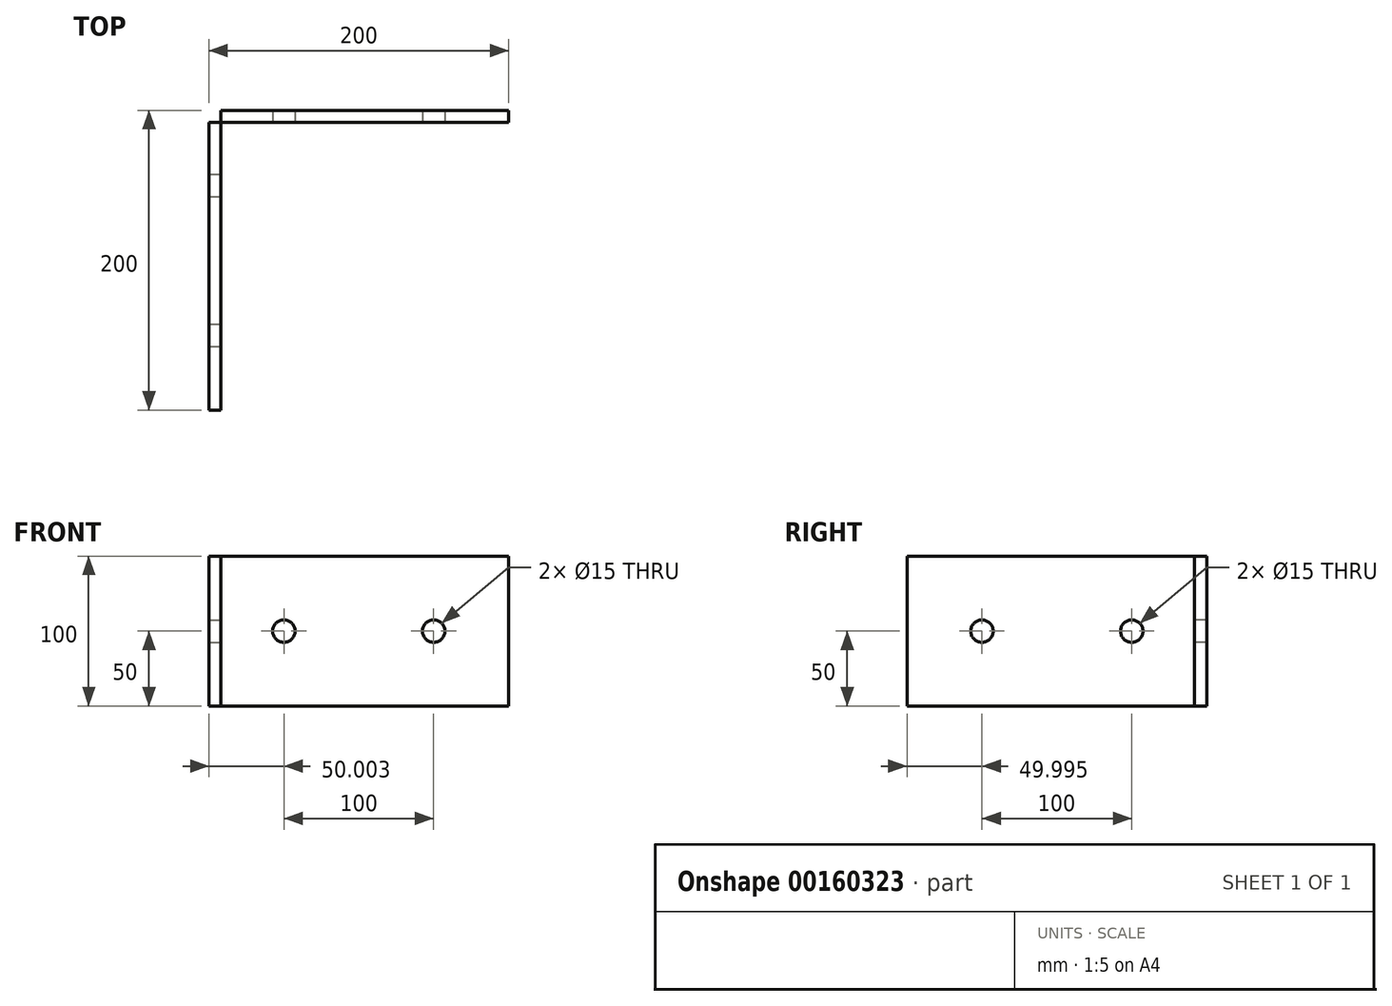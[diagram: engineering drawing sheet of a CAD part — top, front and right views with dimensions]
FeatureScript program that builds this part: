
annotation { "Feature Type Name" : "Feature", "Feature Type Description" : "" }
export const myFeature = defineFeature(function(context is Context, id is Id, definition is map)
    precondition{}
    {
        {
            var Q0;
            Q0=qCreatedBy(makeId("Top.planeOp"),FACE);
            var sketch = newSketch(context, id + "F0", { "sketchPlane" : qUnion([Q0])});
            skLineSegment(sketch, "E0.bottom", {"start": v(-103.35, 122) * mm, "end": v(-95.35, 122) * mm});
            skLineSegment(sketch, "E0.top", {"start": v(-103.35, -78) * mm, "end": v(-95.35, -78) * mm});
            skLineSegment(sketch, "E0.left", {"start": v(-103.35, 122) * mm, "end": v(-103.35, -78) * mm});
            skLineSegment(sketch, "E0.right", {"start": v(-95.35, 122) * mm, "end": v(-95.35, -78) * mm});
            skLineSegment(sketch, "E1.bottom", {"start": v(-103.35, 122) * mm, "end": v(96.65, 122) * mm});
            skLineSegment(sketch, "E1.top", {"start": v(-103.35, 114) * mm, "end": v(96.65, 114) * mm});
            skLineSegment(sketch, "E1.left", {"start": v(-103.35, 122) * mm, "end": v(-103.35, 114) * mm});
            skLineSegment(sketch, "E1.right", {"start": v(96.65, 122) * mm, "end": v(96.65, 114) * mm});
            skSolve(sketch);
        }
        {
            var Q0;
            {var subQ5=sQuery(id+"F0.wireOp",EDGE,"E1.right");Q0=makeQuery(id+"F0.imprint","IMPRINT",FACE,{"disambiguationData":[TD([[makeQuery(id+"F0.imprint","IMPRINT",EDGE,{"derivedFrom":subQ5}),-1.0]])]});}
            var Q1;
            {var subQ5=sQuery(id+"F0.wireOp",EDGE,"E1.left");Q1=makeQuery(id+"F0.imprint","IMPRINT",FACE,{"disambiguationData":[TD([[makeQuery(id+"F0.imprint","IMPRINT",EDGE,{"derivedFrom":subQ5}),1.0]])]});}
            var Q2;
            {var subQ0=sQuery(id+"F0.wireOp",EDGE,"E0.top");Q2=makeQuery(id+"F0.imprint","IMPRINT",FACE,{"disambiguationData":[TD([[makeQuery(id+"F0.imprint","IMPRINT",EDGE,{"derivedFrom":subQ0}),1.0]])]});}
            extrude(context, id + "F1", {"entities" : qUnion([Q0, Q1, Q2]), "depth" : 100 * mm});
        }
        {
            var Q0;
            Q0=makeQuery(id+"F1.opExtrude","SWEPT_FACE",FACE,{"disambiguationData":[OSD([sQuery(id+"F0.wireOp",EDGE,"E1.top")])]});
            var sketch = newSketch(context, id + "F2", { "sketchPlane" : qUnion([Q0])});
            skLineSegment(sketch, "E2.0.0", {"start": v(-95.35, 0) * mm, "end": v(96.65, 0) * mm});
            skLineSegment(sketch, "E2.0.1", {"start": v(96.65, 0) * mm, "end": v(96.65, 100) * mm});
            skLineSegment(sketch, "E2.0.2", {"start": v(96.65, 100) * mm, "end": v(-95.35, 100) * mm});
            skLineSegment(sketch, "E2.0.3", {"start": v(-95.35, 100) * mm, "end": v(-95.35, 0) * mm});
            skCircle(sketch, "E3", {"center": v(-53.35, 50) * mm, "radius": 7.5 * mm});
            skCircle(sketch, "E4", {"center": v(46.65, 50) * mm, "radius": 7.5 * mm});
            skSolve(sketch);
        }
        {
            var Q0;
            Q0=makeQuery(id+"F2.imprint","IMPRINT",FACE,{"disambiguationData":[TD([[makeQuery(id+"F2.imprint","IMPRINT",EDGE,{"derivedFrom":sQuery(id+"F2.wireOp",EDGE,"E3")}),1.0]])]});
            var Q1;
            Q1=makeQuery(id+"F2.imprint","IMPRINT",FACE,{"disambiguationData":[TD([[makeQuery(id+"F2.imprint","IMPRINT",EDGE,{"derivedFrom":sQuery(id+"F2.wireOp",EDGE,"E4")}),1.0]])]});
            extrude(context, id + "F3", {"entities" : qUnion([Q0, Q1]), "operationType" : NewBodyOperationType.REMOVE, "oppositeDirection" : true, "depth" : 8 * mm});
        }
        {
            var Q0;
            Q0=makeQuery(id+"F1.opExtrude","SWEPT_FACE",FACE,{"disambiguationData":[OSD([sQuery(id+"F0.wireOp",EDGE,"E0.right")])]});
            var sketch = newSketch(context, id + "F4", { "sketchPlane" : qUnion([Q0])});
            skLineSegment(sketch, "E5.0.0", {"start": v(-78, 0) * mm, "end": v(114, 0) * mm});
            skLineSegment(sketch, "E5.0.1", {"start": v(114, 0) * mm, "end": v(114, 100) * mm});
            skLineSegment(sketch, "E5.0.2", {"start": v(114, 100) * mm, "end": v(-78, 100) * mm});
            skLineSegment(sketch, "E5.0.3", {"start": v(-78, 100) * mm, "end": v(-78, 0) * mm});
            skCircle(sketch, "E6", {"center": v(-28, 50) * mm, "radius": 7.5 * mm});
            skCircle(sketch, "E7", {"center": v(72, 50) * mm, "radius": 7.5 * mm});
            skSolve(sketch);
        }
        {
            var Q0;
            Q0=makeQuery(id+"F4.imprint","IMPRINT",FACE,{"disambiguationData":[TD([[makeQuery(id+"F4.imprint","IMPRINT",EDGE,{"derivedFrom":sQuery(id+"F4.wireOp",EDGE,"E6")}),1.0]])]});
            var Q1;
            Q1=makeQuery(id+"F4.imprint","IMPRINT",FACE,{"disambiguationData":[TD([[makeQuery(id+"F4.imprint","IMPRINT",EDGE,{"derivedFrom":sQuery(id+"F4.wireOp",EDGE,"E7")}),1.0]])]});
            extrude(context, id + "F5", {"entities" : qUnion([Q0, Q1]), "operationType" : NewBodyOperationType.REMOVE, "oppositeDirection" : true, "depth" : 8 * mm});
        }
    });
